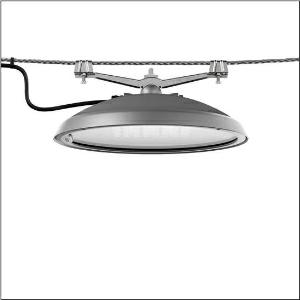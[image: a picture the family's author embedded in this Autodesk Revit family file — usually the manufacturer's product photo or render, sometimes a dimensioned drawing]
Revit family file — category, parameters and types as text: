
# Revit family: dl_r__50_iq_mini___st0_8s_5xa248v31f08fe_ae35
name_source: partatom
category: Lighting Fixtures
units: mm (PartAtom-declared; Revit-internal decimal feet)

## family parameters
Cut with Voids When Loaded = No
Host = Face
Light Source = No
Part Type = Normal
Room Calculation Point = No
Round Connector Dimension = Use Diameter
Shared = No

## types (1)
- --- (1 x LED, 2700 lm, 16.3 W, 3000K)
    Apparent Load = 16 VA
    CIE Flux Codes = 38 75 97 100 100
    Color Rendering = 70
    Color Temperature = 3000K
    Default Elevation = 1800 mm
    Description = DL® 50 iQ mini, catenary luminaire, primary light control with lens, of PMMA, primary optical cover: cover, of toughened safety glass, transparent, light distribution: ST0.8s, light emission: direct distribution, primary light characteristic: symmetric, installation type: suspended mounting, LED, High Power LED, rated luminous flux: 2.700lm, luminous efficacy: 166lm/W, light colour: 730, colour temperature: 3000K, control: optimised constant luminous flux control (CLO 2.0), Desk-Remote (wireless, voltage-free reading and setting of iQ features in the workshop via application-optimized NFC function/RFID function), Light-Fading, Smart-Wire, Night-Set, Lumen-Switch, Temp-Guard, Auto-Match, Street-Remote, mains connection: 230..240V, AC, 50/60Hz, start of lifetime: 16W, end of service life: 17W, reduction: 8W, luminaire housing, of diecast aluminium, powder-coated, Siteco® metallic grey (DB 702S), diameter: 500mm, height: 115mm, protection rating (complete): IP66, insulation class (complete): insulation class II (safety insulation), certification: CE, ENEC, VDE, impact resistance: IK08, permissible operating ambient temperature for outdoor applications: -25..+40°C, standard-compliant lighting for roads and squares, packaging unit: 1 piece

Light Distribution: ST0.8s
    Height = 124 mm  [stored 0.406824 ft]
    Lamp = 1 x LED
    Lamp Light Flux = 2700 lm
    Lamp Power = 16.3 W
    Lamp count = 1
    Length = 500 mm
    Luminous efficacy = 166 lm/W
    Manufacturer = Siteco
    ModVariant = No
    Model = 5XA248V31F08FE
    Number of Poles = 1
    OnlyDefault = Yes
    Power Factor = 1
    Product Name = DL® 50 iQ mini | ST0.8s
    Product group = catenary luminaire
    ProductGroupID = 6300
    Protection Class = Protection class II
    Protection Degree = IP 66
    RLX_Detail_Level = 1
    RLX_Emergency_Light_Flux = 0 lm
    RLX_Emergency_Type = 0
    RLX_Emergency_Type_DB = No
    RlxData = <blob elided: 123549 chars, md5=91b1c691>
    Socket = socket
    Standby Power = 0 W
    System Light Flux = 2700 lm
    System Power = 16 W
    Type Comments = factory setting: luminous flux: 100 % | dim-lin: 254 | 333 mA
    Type Image = l_1242791.jpg
    URL = http://relux.com
    VarID = @adj_069291
    Voltage = 0 V
    Weight = 0.00 kg
    Width = 0 mm  [stored 0 ft]

note: [stored X ft] marks values corroborated as IEEE doubles in the binary element streams (Revit-internal decimal feet)

## geometry (parser evidence)
native form markers: Blend x4, Sweep x13
no freeform markers — native parametric forms only
